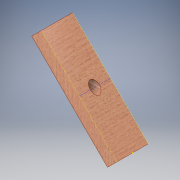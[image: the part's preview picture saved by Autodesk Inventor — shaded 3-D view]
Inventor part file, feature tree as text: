
AUTODESK INVENTOR PART (.ipt)
format: ipt  version: 2019.4 (Build 234330000, 330)  size: 127,488 bytes
history: native  units: in
note: dims shown in document units (in); Inventor stores cm internally (conversion verified against a paired STEP export)
features: sketch x3, extrude x2, plane x1
ambient origin geometry x8: Origin, YZ Plane, XZ Plane, XY Plane, X Axis, Y Axis, Z Axis, Center Point
bodies: Solid1 (feature_tree)
feature tree (6):
  extrude  "Extrusion1"  TaperAngle=45.0deg  [1 undecoded]
  sketch  "Sketch3"  dims[d4=1.5in d5=45.0deg]
  plane  "Work Plane1"
  extrude  "Extrusion2"  TaperAngle=45.0deg  [1 undecoded]
  sketch  "Sketch1"  dims[d1=135.0deg d3=45.0deg]
  sketch  "Sketch4"  dims[d7=0.0in d8=90.0deg d17=1.0in d18=1.0in d19=0.0in]
note: 2 required parameter values undecoded (feature->parameter linkage not recoverable at this tier; creation-order binding heuristic only, values carry confidence <= 0.55)
